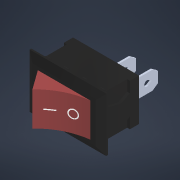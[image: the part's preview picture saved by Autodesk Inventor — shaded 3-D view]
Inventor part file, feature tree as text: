
AUTODESK INVENTOR PART (.ipt)
format: ipt  version: 2021 (Build 250183000, 183)  size: 224,256 bytes
history: native  units: mm
features: chamfer x1
ambient origin geometry x8: Origin, YZ Plane, XZ Plane, XY Plane, X Axis, Y Axis, Z Axis, Center Point
bodies: Solid1 (feature_tree)
feature tree (1):
  chamfer  "Chamfer2"  [1 undecoded]
note: 1 required parameter value undecoded (feature->parameter linkage not recoverable at this tier; creation-order binding heuristic only, values carry confidence <= 0.55)
